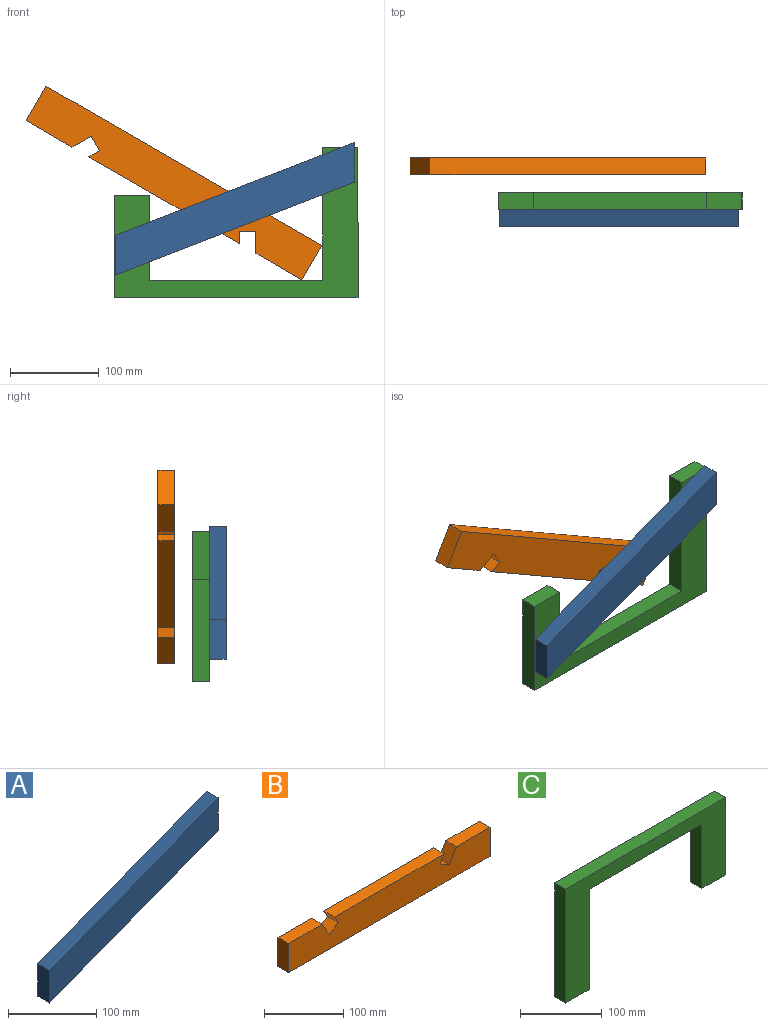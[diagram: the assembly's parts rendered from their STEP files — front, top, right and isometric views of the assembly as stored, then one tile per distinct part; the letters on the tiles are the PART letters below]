
ASSEMBLY  parts=3 mates=1
PART A: 6 faces, bbox 270.3x19x150 mm
  f0: plane 270.32x105mm, normal (-0.36,0,0.93), area 5510mm2, adj f1,f3,f4,f5
  f1: plane 45x19mm, normal (-1,0,0), area 855mm2, adj f0,f2,f4,f5
  f2: plane 270.32x105mm, normal (0.36,0,-0.93), area 5510mm2, adj f1,f3,f4,f5
  f3: plane 45x19mm, normal (1,0,0), area 855mm2, adj f0,f2,f4,f5
  f4: plane 270.32x150mm, normal (0,-1,0), area 12164.6mm2, adj f0,f1,f2,f3
  f5: plane 270.32x150mm, normal (0,1,0), area 12164.6mm2, adj f0,f1,f2,f3
PART B: 14 faces, bbox 360x19x45 mm
  f0: plane 196.12x19mm, normal (0,0,1), area 3726.3mm2, adj f1,f11,f12,f13
  f1: plane 19x12.15mm, normal (-0.87,0,-0.5), area 266.6mm2, adj f0,f2,f12,f13
  f2: plane 19x16.45mm, normal (-0.5,0,0.87), area 361mm2, adj f1,f3,f12,f13
  f3: plane 21.65x19mm, normal (0.87,0,0.5), area 475mm2, adj f2,f4,f12,f13
  f4: plane 60x19mm, normal (0,0,1), area 1140mm2, adj f3,f5,f12,f13
  f5: plane 45x19mm, normal (-1,0,0), area 855mm2, adj f4,f6,f12,f13
  f6: plane 360x19mm, normal (0,0,-1), area 6840mm2, adj f5,f7,f12,f13
  f7: plane 45x19mm, normal (1,0,0), area 855mm2, adj f6,f8,f12,f13
  f8: plane 60x19mm, normal (0,0,1), area 1140mm2, adj f7,f9,f12,f13
  f9: plane 21.65x19mm, normal (-0.87,0,0.5), area 475mm2, adj f8,f10,f12,f13
  f10: plane 19x16.45mm, normal (0.5,0,0.87), area 361mm2, adj f9,f11,f12,f13
  f11: plane 19x12.15mm, normal (0.87,0,-0.5), area 266.6mm2, adj f0,f10,f12,f13
  f12: plane 360x45mm, normal (0,-1,0), area 15458.4mm2, adj f0,f1,f2,f3,f4,f5,f6,f7
  f13: plane 360x45mm, normal (0,1,0), area 15458.4mm2, adj f0,f1,f2,f3,f4,f5,f6,f7
PART C: 10 faces, bbox 275x19x170 mm
  f0: plane 150x19mm, normal (1,0,0), area 2850mm2, adj f1,f7,f8,f9
  f1: plane 195x19mm, normal (0,0,-1), area 3705mm2, adj f0,f2,f8,f9
  f2: plane 96x19mm, normal (-1,0,0), area 1824mm2, adj f1,f3,f8,f9
  f3: plane 40x19mm, normal (0,0,-1), area 760mm2, adj f2,f4,f8,f9
  f4: plane 116x19mm, normal (1,0,0), area 2204mm2, adj f3,f5,f8,f9
  f5: plane 275x19mm, normal (0,0,1), area 5225mm2, adj f4,f6,f8,f9
  f6: plane 170x19mm, normal (-1,0,0), area 3230mm2, adj f5,f7,f8,f9
  f7: plane 40x19mm, normal (0,0,-1), area 760mm2, adj f0,f6,f8,f9
  f8: plane 275x170mm, normal (0,-1,0), area 15340mm2, adj f0,f1,f2,f3,f4,f5,f6,f7
  f9: plane 275x170mm, normal (0,1,0), area 15340mm2, adj f0,f1,f2,f3,f4,f5,f6,f7
PLACE A rot(axis=(0,1,0),180deg) t=(324.03,-36.56,-348.66)mm
PLACE B rot(axis=(0,-1,0),150deg) t=(264.51,2.61,-353.97)mm
PLACE C rot(axis=(0,1,0),180deg) t=(327.83,-36.56,-354.43)mm
MATE fastened A.f5 <-> C.f8  axis (0,1,0) through (188.87,-55.56,-273.66)mm
